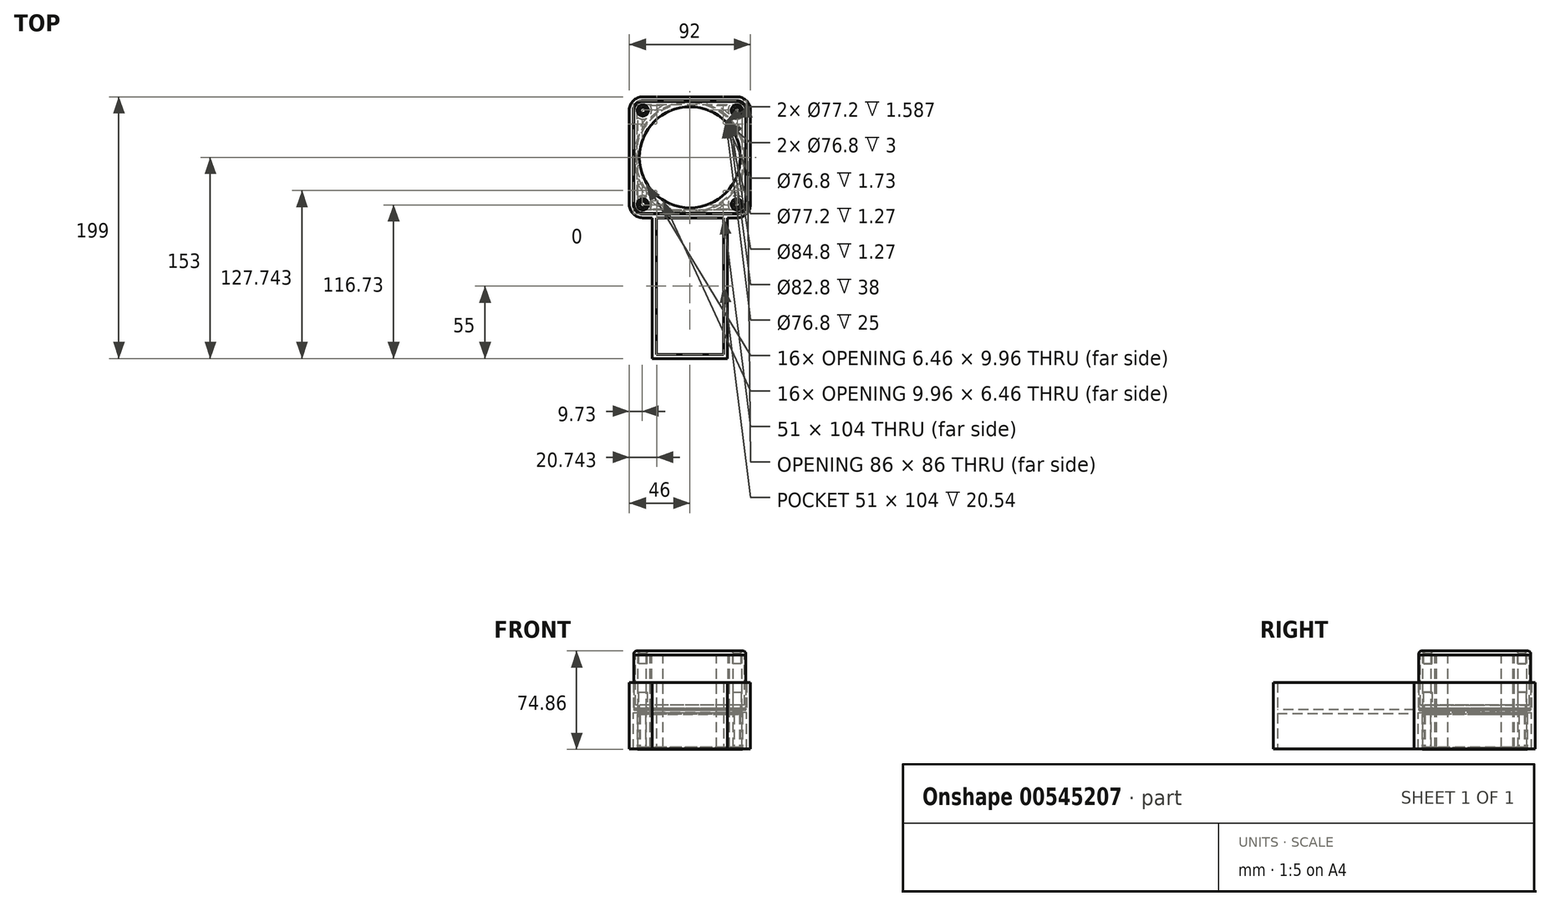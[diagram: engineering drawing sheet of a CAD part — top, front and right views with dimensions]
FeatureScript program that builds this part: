
annotation { "Feature Type Name" : "Feature", "Feature Type Description" : "" }
export const myFeature = defineFeature(function(context is Context, id is Id, definition is map)
    precondition{}
    {
        {
            var Q0;
            Q0=qCreatedBy(makeId("Top.planeOp"),FACE);
            var sketch = newSketch(context, id + "F0", { "sketchPlane" : qUnion([Q0])});
            skCircle(sketch, "E0", {"center": v(0, 0) * mm, "radius": 38.4 * mm});
            skLineSegment(sketch, "E1.bottom", {"start": v(40, -40) * mm, "end": v(-40, -40) * mm});
            skLineSegment(sketch, "E1.top", {"start": v(40, 40) * mm, "end": v(-40, 40) * mm});
            skLineSegment(sketch, "E1.left", {"start": v(40, -40) * mm, "end": v(40, 40) * mm});
            skLineSegment(sketch, "E1.right", {"start": v(-40, -40) * mm, "end": v(-40, 40) * mm});
            skLineSegment(sketch, "E2", {"start": v(0, 36.26) * mm, "end": v(0, 0) * mm, "construction": true});
            skLineSegment(sketch, "E3", {"start": v(0, 0) * mm, "end": v(31.67, 0) * mm, "construction": true});
            skCircle(sketch, "E4", {"center": v(-35.75, 35.75) * mm, "radius": 2.1 * mm});
            skCircle(sketch, "E5.MirrorC", {"center": v(35.75, 35.75) * mm, "radius": 2.1 * mm});
            skCircle(sketch, "E6.MirrorC", {"center": v(35.75, -35.75) * mm, "radius": 2.1 * mm});
            skCircle(sketch, "E7.MirrorC", {"center": v(-35.75, -35.75) * mm, "radius": 2.1 * mm});
            skSolve(sketch);
        }
        {
            var Q0;
            Q0 = qSketchRegion(id + "F0", true);
            extrude(context, id + "F1", {"entities" : qUnion([Q0]), "depth" : 25 * mm, "offsetDistance" : 25 * mm});
        }
        {
            var Q0;
            Q0=makeQuery(id+"F1.opExtrude","CAP_FACE",FACE,{"disambiguationData":[OSD([sQuery(id+"F0.wireOp",EDGE,"E0"),sQuery(id+"F0.wireOp",EDGE,"E1.bottom"),sQuery(id+"F0.wireOp",EDGE,"E1.top"),sQuery(id+"F0.wireOp",EDGE,"E1.left"),sQuery(id+"F0.wireOp",EDGE,"E1.right"),sQuery(id+"F0.wireOp",EDGE,"E4"),sQuery(id+"F0.wireOp",EDGE,"E5.MirrorC"),sQuery(id+"F0.wireOp",EDGE,"E6.MirrorC"),sQuery(id+"F0.wireOp",EDGE,"E7.MirrorC")])],"isStart":false});
            var sketch = newSketch(context, id + "F2", { "sketchPlane" : qUnion([Q0])});
            skCircle(sketch, "E8.0", {"center": v(0, 0) * mm, "radius": 38.6 * mm});
            skLineSegment(sketch, "E9.0", {"start": v(39.8, -39.8) * mm, "end": v(39.8, 39.8) * mm});
            skLineSegment(sketch, "E9.1", {"start": v(-39.8, -39.8) * mm, "end": v(39.8, -39.8) * mm});
            skLineSegment(sketch, "E9.2", {"start": v(-39.8, 39.8) * mm, "end": v(-39.8, -39.8) * mm});
            skLineSegment(sketch, "E9.3", {"start": v(39.8, 39.8) * mm, "end": v(-39.8, 39.8) * mm});
            skCircle(sketch, "E10.0", {"center": v(-35.75, 35.75) * mm, "radius": 2.3 * mm});
            skCircle(sketch, "E11.0", {"center": v(35.75, 35.75) * mm, "radius": 2.3 * mm});
            skCircle(sketch, "E12.0", {"center": v(35.75, -35.75) * mm, "radius": 2.3 * mm});
            skCircle(sketch, "E13.0", {"center": v(-35.75, -35.75) * mm, "radius": 2.3 * mm});
            skSolve(sketch);
        }
        {
            var Q0;
            Q0 = qSketchRegion(id + "F2", true);
            extrude(context, id + "F3", {"entities" : qUnion([Q0]), "depth" : 1.59 * mm, "offsetDistance" : 25 * mm});
        }
        {
            var Q0;
            Q0=makeQuery(id+"F1.opExtrude","CAP_FACE",FACE,{"disambiguationData":[OSD([sQuery(id+"F0.wireOp",EDGE,"E0"),sQuery(id+"F0.wireOp",EDGE,"E1.bottom"),sQuery(id+"F0.wireOp",EDGE,"E1.top"),sQuery(id+"F0.wireOp",EDGE,"E1.left"),sQuery(id+"F0.wireOp",EDGE,"E1.right"),sQuery(id+"F0.wireOp",EDGE,"E4"),sQuery(id+"F0.wireOp",EDGE,"E5.MirrorC"),sQuery(id+"F0.wireOp",EDGE,"E6.MirrorC"),sQuery(id+"F0.wireOp",EDGE,"E7.MirrorC")])],"isStart":true});
            var sketch = newSketch(context, id + "F4", { "sketchPlane" : qUnion([Q0])});
            skCircle(sketch, "E14.0", {"center": v(0, 0) * mm, "radius": 38.6 * mm});
            skLineSegment(sketch, "E14.1", {"start": v(39.8, 39.8) * mm, "end": v(39.8, -39.8) * mm});
            skLineSegment(sketch, "E14.2", {"start": v(-39.8, 39.8) * mm, "end": v(39.8, 39.8) * mm});
            skLineSegment(sketch, "E14.3", {"start": v(-39.8, -39.8) * mm, "end": v(-39.8, 39.8) * mm});
            skLineSegment(sketch, "E14.4", {"start": v(39.8, -39.8) * mm, "end": v(-39.8, -39.8) * mm});
            skCircle(sketch, "E14.5", {"center": v(-35.75, -35.75) * mm, "radius": 2.3 * mm});
            skCircle(sketch, "E14.6", {"center": v(35.75, -35.75) * mm, "radius": 2.3 * mm});
            skCircle(sketch, "E14.7", {"center": v(35.75, 35.75) * mm, "radius": 2.3 * mm});
            skCircle(sketch, "E14.8", {"center": v(-35.75, 35.75) * mm, "radius": 2.3 * mm});
            skSolve(sketch);
        }
        {
            var Q0;
            Q0 = qSketchRegion(id + "F4", true);
            extrude(context, id + "F5", {"entities" : qUnion([Q0]), "depth" : 1.59 * mm, "offsetDistance" : 25 * mm});
        }
        {
            var Q0;
            Q0=makeQuery(id+"F3.opExtrude","CAP_FACE",FACE,{"disambiguationData":[OSD([sQuery(id+"F2.wireOp",EDGE,"E8.0"),sQuery(id+"F2.wireOp",EDGE,"E9.0"),sQuery(id+"F2.wireOp",EDGE,"E9.1"),sQuery(id+"F2.wireOp",EDGE,"E9.2"),sQuery(id+"F2.wireOp",EDGE,"E9.3"),sQuery(id+"F2.wireOp",EDGE,"E10.0"),sQuery(id+"F2.wireOp",EDGE,"E11.0"),sQuery(id+"F2.wireOp",EDGE,"E12.0"),sQuery(id+"F2.wireOp",EDGE,"E13.0")])],"isStart":false});
            cPlane(context, id + "F6", {"entities" : qUnion([Q0]), "cplaneType" : CPlaneType.OFFSET, "offset" : 0.32 * mm, "oppositeDirection" : true, "width" : 150 * mm, "height" : 150 * mm});
        }
        {
            var Q0;
            Q0=makeQuery(id+"F5.opExtrude","CAP_FACE",FACE,{"disambiguationData":[OSD([sQuery(id+"F4.wireOp",EDGE,"E14.0"),sQuery(id+"F4.wireOp",EDGE,"E14.1"),sQuery(id+"F4.wireOp",EDGE,"E14.2"),sQuery(id+"F4.wireOp",EDGE,"E14.3"),sQuery(id+"F4.wireOp",EDGE,"E14.4"),sQuery(id+"F4.wireOp",EDGE,"E14.5"),sQuery(id+"F4.wireOp",EDGE,"E14.6"),sQuery(id+"F4.wireOp",EDGE,"E14.7"),sQuery(id+"F4.wireOp",EDGE,"E14.8")])],"isStart":false});
            cPlane(context, id + "F7", {"entities" : qUnion([Q0]), "cplaneType" : CPlaneType.OFFSET, "offset" : 0.32 * mm, "oppositeDirection" : true, "width" : 150 * mm, "height" : 150 * mm});
        }
        {
            var Q0;
            Q0=qCreatedBy(id+"F6.planeOp",FACE);
            var sketch = newSketch(context, id + "F8", { "sketchPlane" : qUnion([Q0])});
            skLineSegment(sketch, "E15.bottom", {"start": v(-43, 43) * mm, "end": v(43, 43) * mm});
            skLineSegment(sketch, "E15.top", {"start": v(-43, -43) * mm, "end": v(43, -43) * mm});
            skLineSegment(sketch, "E15.left", {"start": v(-43, 43) * mm, "end": v(-43, -43) * mm});
            skLineSegment(sketch, "E15.right", {"start": v(43, 43) * mm, "end": v(43, -43) * mm});
            skPoint(sketch, "E15.middle", {"position": v(0, 0) * mm});
            skLineSegment(sketch, "E16.0", {"start": v(-46, 46) * mm, "end": v(46, 46) * mm});
            skLineSegment(sketch, "E16.1", {"start": v(-46, 46) * mm, "end": v(-46, -46) * mm});
            skLineSegment(sketch, "E16.2", {"start": v(-46, -46) * mm, "end": v(46, -46) * mm});
            skLineSegment(sketch, "E16.3", {"start": v(46, 46) * mm, "end": v(46, -46) * mm});
            skSolve(sketch);
        }
        {
            var Q0;
            Q0 = qSketchRegion(id + "F8", true);
            var Q1;
            Q1=qCreatedBy(id+"F7.planeOp",FACE);
            extrude(context, id + "F9", {"entities" : qUnion([Q0]), "endBound" : BoundingType.UP_TO_SURFACE, "oppositeDirection" : true, "depth" : 3 * mm, "endBoundEntityFace" : qUnion([Q1]), "offsetDistance" : 25 * mm});
        }
        {
            var Q0;
            Q0=makeQuery(id+"F9.opExtrude","CAP_FACE",FACE,{"disambiguationData":[OSD([sQuery(id+"F8.wireOp",EDGE,"E15.bottom"),sQuery(id+"F8.wireOp",EDGE,"E15.top"),sQuery(id+"F8.wireOp",EDGE,"E15.left"),sQuery(id+"F8.wireOp",EDGE,"E15.right"),sQuery(id+"F8.wireOp",EDGE,"E16.0"),sQuery(id+"F8.wireOp",EDGE,"E16.1"),sQuery(id+"F8.wireOp",EDGE,"E16.2"),sQuery(id+"F8.wireOp",EDGE,"E16.3")])],"isStart":true});
            var sketch = newSketch(context, id + "F10", { "sketchPlane" : qUnion([Q0])});
            skCircle(sketch, "E17.0", {"center": v(0, 0) * mm, "radius": 38.4 * mm});
            skLineSegment(sketch, "E18.0", {"start": v(-46, 46) * mm, "end": v(-46, -46) * mm});
            skLineSegment(sketch, "E18.1", {"start": v(-46, 46) * mm, "end": v(46, 46) * mm});
            skLineSegment(sketch, "E18.2", {"start": v(46, 46) * mm, "end": v(46, -46) * mm});
            skLineSegment(sketch, "E18.3", {"start": v(-46, -46) * mm, "end": v(46, -46) * mm});
            skCircle(sketch, "E19.0", {"center": v(0, 0) * mm, "radius": 41.4 * mm, "construction": true});
            skCircle(sketch, "E20.0", {"center": v(-35.75, 35.75) * mm, "radius": 2.3 * mm});
            skCircle(sketch, "E20.1", {"center": v(35.75, 35.75) * mm, "radius": 2.3 * mm});
            skCircle(sketch, "E20.2", {"center": v(35.75, -35.75) * mm, "radius": 2.3 * mm});
            skCircle(sketch, "E20.3", {"center": v(-35.75, -35.75) * mm, "radius": 2.3 * mm});
            skSolve(sketch);
        }
        {
            var Q0;
            Q0 = qSketchRegion(id + "F10", true);
            extrude(context, id + "F11", {"entities" : qUnion([Q0]), "operationType" : NewBodyOperationType.ADD, "depth" : 3 * mm, "offsetDistance" : 25 * mm});
        }
        {
            var Q0;
            Q0=makeQuery(id+"F11.opExtrude","CAP_EDGE",EDGE,{"disambiguationData":[OSD([sQuery(id+"F10.wireOp",EDGE,"E20.1")])],"isStart":false});
            var Q1;
            Q1=makeQuery(id+"F11.opExtrude","CAP_EDGE",EDGE,{"disambiguationData":[OSD([sQuery(id+"F10.wireOp",EDGE,"E20.2")])],"isStart":false});
            var Q2;
            Q2=makeQuery(id+"F11.opExtrude","CAP_EDGE",EDGE,{"disambiguationData":[OSD([sQuery(id+"F10.wireOp",EDGE,"E20.3")])],"isStart":false});
            var Q3;
            Q3=makeQuery(id+"F11.opExtrude","CAP_EDGE",EDGE,{"disambiguationData":[OSD([sQuery(id+"F10.wireOp",EDGE,"E20.0")])],"isStart":false});
            chamfer(context, id + "F12", {"entities" : qUnion([Q0, Q1, Q2, Q3]), "width" : 2 * mm, "tangentPropagation" : true});
        }
        {
            var Q0;
            Q0=makeQuery(id+"F11.opExtrude","CAP_FACE",FACE,{"disambiguationData":[OSD([sQuery(id+"F10.wireOp",EDGE,"E17.0"),sQuery(id+"F10.wireOp",EDGE,"E18.0"),sQuery(id+"F10.wireOp",EDGE,"E18.1"),sQuery(id+"F10.wireOp",EDGE,"E18.2"),sQuery(id+"F10.wireOp",EDGE,"E18.3"),sQuery(id+"F10.wireOp",EDGE,"E20.0"),sQuery(id+"F10.wireOp",EDGE,"E20.1"),sQuery(id+"F10.wireOp",EDGE,"E20.2"),sQuery(id+"F10.wireOp",EDGE,"E20.3")])],"isStart":false});
            var sketch = newSketch(context, id + "F13", { "sketchPlane" : qUnion([Q0])});
            skLineSegment(sketch, "E21.0.0", {"start": v(46, -46) * mm, "end": v(46, 46) * mm});
            skLineSegment(sketch, "E21.0.1", {"start": v(46, 46) * mm, "end": v(-46, 46) * mm});
            skLineSegment(sketch, "E21.0.2", {"start": v(-46, 46) * mm, "end": v(-46, -46) * mm});
            skLineSegment(sketch, "E21.0.3", {"start": v(-46, -46) * mm, "end": v(46, -46) * mm});
            skLineSegment(sketch, "E22.0", {"start": v(43, -43) * mm, "end": v(43, 43) * mm});
            skLineSegment(sketch, "E22.1", {"start": v(-43, -43) * mm, "end": v(43, -43) * mm});
            skLineSegment(sketch, "E22.2", {"start": v(-43, 43) * mm, "end": v(-43, -43) * mm});
            skLineSegment(sketch, "E22.3", {"start": v(43, 43) * mm, "end": v(-43, 43) * mm});
            skSolve(sketch);
        }
        {
            var Q0;
            Q0 = qSketchRegion(id + "F13", true);
            extrude(context, id + "F14", {"entities" : qUnion([Q0]), "operationType" : NewBodyOperationType.ADD, "depth" : 20 * mm, "offsetDistance" : 25 * mm});
        }
        {
            var Q0;
            Q0=makeQuery(id+"F11.opExtrude","CAP_FACE",FACE,{"disambiguationData":[OSD([sQuery(id+"F10.wireOp",EDGE,"E17.0"),sQuery(id+"F10.wireOp",EDGE,"E18.0"),sQuery(id+"F10.wireOp",EDGE,"E18.1"),sQuery(id+"F10.wireOp",EDGE,"E18.2"),sQuery(id+"F10.wireOp",EDGE,"E18.3"),sQuery(id+"F10.wireOp",EDGE,"E20.0"),sQuery(id+"F10.wireOp",EDGE,"E20.1"),sQuery(id+"F10.wireOp",EDGE,"E20.2"),sQuery(id+"F10.wireOp",EDGE,"E20.3")])],"isStart":false});
            var sketch = newSketch(context, id + "F15", { "sketchPlane" : qUnion([Q0])});
            skCircle(sketch, "E23.0", {"center": v(0, 0) * mm, "radius": 38.4 * mm});
            skCircle(sketch, "E24.0", {"center": v(0, 0) * mm, "radius": 42.4 * mm});
            skSolve(sketch);
        }
        {
            var Q0;
            Q0 = qSketchRegion(id + "F15", true);
            extrude(context, id + "F16", {"entities" : qUnion([Q0]), "operationType" : NewBodyOperationType.REMOVE, "oppositeDirection" : true, "depth" : 1.59 * mm - 0.32 * mm, "offsetDistance" : 25 * mm});
        }
        {
            var Q0;
            Q0=makeQuery(id+"F16.boolean.opBoolean","COPY",FACE,{"derivedFrom":makeQuery(id+"F16.opExtrude","CAP_FACE",FACE,{"disambiguationData":[OSD([sQuery(id+"F15.wireOp",EDGE,"E23.0"),sQuery(id+"F15.wireOp",EDGE,"E24.0")])],"isStart":false})});
            var sketch = newSketch(context, id + "F17", { "sketchPlane" : qUnion([Q0])});
            skCircle(sketch, "E25.0", {"center": v(0, 0) * mm, "radius": 42.2 * mm});
            skCircle(sketch, "E26.0", {"center": v(0, 0) * mm, "radius": 38.6 * mm});
            skSolve(sketch);
        }
        {
            var Q0;
            Q0 = qSketchRegion(id + "F17", true);
            extrude(context, id + "F18", {"entities" : qUnion([Q0]), "depth" : 1.59 * mm, "offsetDistance" : 25 * mm});
        }
        {
            var Q0;
            Q0=makeQuery(id+"F11.opExtrude","CAP_FACE",FACE,{"disambiguationData":[OSD([sQuery(id+"F10.wireOp",EDGE,"E17.0"),sQuery(id+"F10.wireOp",EDGE,"E18.0"),sQuery(id+"F10.wireOp",EDGE,"E18.1"),sQuery(id+"F10.wireOp",EDGE,"E18.2"),sQuery(id+"F10.wireOp",EDGE,"E18.3"),sQuery(id+"F10.wireOp",EDGE,"E20.0"),sQuery(id+"F10.wireOp",EDGE,"E20.1"),sQuery(id+"F10.wireOp",EDGE,"E20.2"),sQuery(id+"F10.wireOp",EDGE,"E20.3")])],"isStart":false});
            var sketch = newSketch(context, id + "F19", { "sketchPlane" : qUnion([Q0])});
            skLineSegment(sketch, "E27.0", {"start": v(42.5, -42.5) * mm, "end": v(42.5, 42.5) * mm});
            skLineSegment(sketch, "E27.1", {"start": v(-42.5, -42.5) * mm, "end": v(42.5, -42.5) * mm});
            skLineSegment(sketch, "E27.2", {"start": v(-42.5, 42.5) * mm, "end": v(-42.5, -42.5) * mm});
            skLineSegment(sketch, "E27.3", {"start": v(42.5, 42.5) * mm, "end": v(-42.5, 42.5) * mm});
            skCircle(sketch, "E28.0", {"center": v(0, 0) * mm, "radius": 38.4 * mm});
            skSolve(sketch);
        }
        {
            var Q0;
            Q0 = qSketchRegion(id + "F19", true);
            extrude(context, id + "F20", {"entities" : qUnion([Q0]), "depth" : 41 * mm, "offsetDistance" : 25 * mm});
        }
        {
            var Q0;
            Q0=makeQuery(id+"F20.opExtrude","CAP_FACE",FACE,{"disambiguationData":[OSD([sQuery(id+"F19.wireOp",EDGE,"E27.0"),sQuery(id+"F19.wireOp",EDGE,"E27.1"),sQuery(id+"F19.wireOp",EDGE,"E27.2"),sQuery(id+"F19.wireOp",EDGE,"E27.3"),sQuery(id+"F19.wireOp",EDGE,"E28.0")])],"isStart":false});
            var sketch = newSketch(context, id + "F21", { "sketchPlane" : qUnion([Q0])});
            skCircle(sketch, "E29.0", {"center": v(0, 0) * mm, "radius": 41.4 * mm});
            skSolve(sketch);
        }
        {
            var Q0;
            Q0 = qSketchRegion(id + "F21", true);
            extrude(context, id + "F22", {"entities" : qUnion([Q0]), "operationType" : NewBodyOperationType.REMOVE, "oppositeDirection" : true, "depth" : 38 * mm, "offsetDistance" : 25 * mm});
        }
        {
            var Q0;
            Q0=makeQuery(id+"F20.opExtrude","CAP_FACE",FACE,{"disambiguationData":[OSD([sQuery(id+"F19.wireOp",EDGE,"E27.0"),sQuery(id+"F19.wireOp",EDGE,"E27.1"),sQuery(id+"F19.wireOp",EDGE,"E27.2"),sQuery(id+"F19.wireOp",EDGE,"E27.3"),sQuery(id+"F19.wireOp",EDGE,"E28.0")])],"isStart":true});
            var sketch = newSketch(context, id + "F23", { "sketchPlane" : qUnion([Q0])});
            skCircle(sketch, "E30", {"center": v(35.75, -35.75) * mm, "radius": 3.25 * mm});
            skCircle(sketch, "E31", {"center": v(-35.75, 35.75) * mm, "radius": 3.25 * mm});
            skCircle(sketch, "E32", {"center": v(-35.75, -35.75) * mm, "radius": 3.25 * mm});
            skCircle(sketch, "E33", {"center": v(35.75, 35.75) * mm, "radius": 3.25 * mm});
            skSolve(sketch);
        }
        {
            var Q0;
            Q0 = qSketchRegion(id + "F23", true);
            extrude(context, id + "F24", {"entities" : qUnion([Q0]), "operationType" : NewBodyOperationType.REMOVE, "oppositeDirection" : true, "depth" : 12.7 * mm, "offsetDistance" : 25 * mm});
        }
        {
            var Q0;
            Q0=makeQuery(id+"F20.opExtrude","CAP_FACE",FACE,{"disambiguationData":[OSD([sQuery(id+"F19.wireOp",EDGE,"E27.0"),sQuery(id+"F19.wireOp",EDGE,"E27.1"),sQuery(id+"F19.wireOp",EDGE,"E27.2"),sQuery(id+"F19.wireOp",EDGE,"E27.3"),sQuery(id+"F19.wireOp",EDGE,"E28.0")])],"isStart":false});
            var sketch = newSketch(context, id + "F25", { "sketchPlane" : qUnion([Q0])});
            skCircle(sketch, "E34", {"center": v(-35.75, 35.75) * mm, "radius": 3.15 * mm});
            skCircle(sketch, "E35", {"center": v(35.75, 35.75) * mm, "radius": 3.15 * mm});
            skCircle(sketch, "E36", {"center": v(35.75, -35.75) * mm, "radius": 3.15 * mm});
            skCircle(sketch, "E37", {"center": v(-35.75, -35.75) * mm, "radius": 3.15 * mm});
            skSolve(sketch);
        }
        {
            var Q0;
            Q0 = qSketchRegion(id + "F25", true);
            extrude(context, id + "F26", {"entities" : qUnion([Q0]), "operationType" : NewBodyOperationType.REMOVE, "oppositeDirection" : true, "depth" : 6.7 * mm, "offsetDistance" : 25 * mm});
        }
        {
            var Q0;
            Q0=makeQuery(id+"F20.opExtrude","CAP_FACE",FACE,{"disambiguationData":[OSD([sQuery(id+"F19.wireOp",EDGE,"E27.0"),sQuery(id+"F19.wireOp",EDGE,"E27.1"),sQuery(id+"F19.wireOp",EDGE,"E27.2"),sQuery(id+"F19.wireOp",EDGE,"E27.3"),sQuery(id+"F19.wireOp",EDGE,"E28.0")])],"isStart":false});
            var sketch = newSketch(context, id + "F27", { "sketchPlane" : qUnion([Q0])});
            skCircle(sketch, "E38", {"center": v(-35.75, 35.75) * mm, "radius": 3.67 * mm});
            skCircle(sketch, "E39", {"center": v(-35.75, -35.75) * mm, "radius": 3.67 * mm});
            skCircle(sketch, "E40", {"center": v(35.75, -35.75) * mm, "radius": 3.67 * mm});
            skCircle(sketch, "E41", {"center": v(35.75, 35.75) * mm, "radius": 3.67 * mm});
            skCircle(sketch, "E42.cCircle", {"center": v(-35.75, 35.75) * mm, "radius": 3.17 * mm, "construction": true});
            skLineSegment(sketch, "E42.0", {"start": v(-33.92, 32.58) * mm, "end": v(-37.58, 32.58) * mm, "construction": true});
            skLineSegment(sketch, "E42.1", {"start": v(-37.58, 32.58) * mm, "end": v(-39.42, 35.75) * mm, "construction": true});
            skLineSegment(sketch, "E42.2", {"start": v(-39.42, 35.75) * mm, "end": v(-37.58, 38.93) * mm, "construction": true});
            skLineSegment(sketch, "E42.3", {"start": v(-37.58, 38.93) * mm, "end": v(-33.92, 38.93) * mm, "construction": true});
            skLineSegment(sketch, "E42.4", {"start": v(-33.92, 38.93) * mm, "end": v(-32.08, 35.75) * mm, "construction": true});
            skLineSegment(sketch, "E42.5", {"start": v(-32.08, 35.75) * mm, "end": v(-33.92, 32.58) * mm, "construction": true});
            skPoint(sketch, "E42.0.midPoint", {"position": v(-35.75, 32.58) * mm});
            skSolve(sketch);
        }
        {
            var Q0;
            Q0 = qSketchRegion(id + "F27", true);
            extrude(context, id + "F28", {"entities" : qUnion([Q0]), "operationType" : NewBodyOperationType.REMOVE, "oppositeDirection" : true, "depth" : .5 * mm, "offsetDistance" : 25 * mm});
        }
        {
            var Q0;
            Q0=makeQuery(id+"F20.opExtrude","CAP_FACE",FACE,{"disambiguationData":[OSD([sQuery(id+"F19.wireOp",EDGE,"E27.0"),sQuery(id+"F19.wireOp",EDGE,"E27.1"),sQuery(id+"F19.wireOp",EDGE,"E27.2"),sQuery(id+"F19.wireOp",EDGE,"E27.3"),sQuery(id+"F19.wireOp",EDGE,"E28.0")])],"isStart":false});
            var sketch = newSketch(context, id + "F29", { "sketchPlane" : qUnion([Q0])});
            skArc(sketch, "E43.0", {"start": v(-39.5, 30.24) * mm, "mid": v(-36.35, 29.11) * mm, "end": v(-33.04, 29.66) * mm});
            skLineSegment(sketch, "E44.0", {"start": v(-39.5, 30.24) * mm, "end": v(-39.5, 20.28) * mm});
            skLineSegment(sketch, "E45.trimOffspring", {"start": v(-39.5, -20.28) * mm, "end": v(-39.5, -42.5) * mm});
            skArc(sketch, "E46.trimOffspring", {"start": v(-29.66, 33.04) * mm, "mid": v(-29.11, 36.35) * mm, "end": v(-30.24, 39.5) * mm});
            skArc(sketch, "E47.trimOffspring", {"start": v(-33.04, 29.66) * mm, "mid": v(-36.57, 25.18) * mm, "end": v(-39.5, 20.28) * mm});
            skArc(sketch, "E48.trimOffspring", {"start": v(-20.28, 39.5) * mm, "mid": v(-25.18, 36.57) * mm, "end": v(-29.66, 33.04) * mm});
            skLineSegment(sketch, "E49.trimOffspring", {"start": v(-20.28, 39.5) * mm, "end": v(-30.24, 39.5) * mm});
            skArc(sketch, "E50.1.0", {"start": v(-39.5, -20.28) * mm, "mid": v(-36.57, -25.18) * mm, "end": v(-33.04, -29.66) * mm});
            skLineSegment(sketch, "E50.1.1", {"start": v(-30.24, -39.5) * mm, "end": v(-20.28, -39.5) * mm});
            skArc(sketch, "E50.1.2", {"start": v(-30.24, -39.5) * mm, "mid": v(-29.11, -36.35) * mm, "end": v(-29.66, -33.04) * mm});
            skArc(sketch, "E50.1.3", {"start": v(-29.66, -33.04) * mm, "mid": v(-25.18, -36.57) * mm, "end": v(-20.28, -39.5) * mm});
            skArc(sketch, "E50.1.4", {"start": v(-33.04, -29.66) * mm, "mid": v(-36.35, -29.11) * mm, "end": v(-39.5, -30.24) * mm});
            skLineSegment(sketch, "E50.1.5", {"start": v(-39.5, -20.28) * mm, "end": v(-39.5, -30.24) * mm});
            skArc(sketch, "E50.2.0", {"start": v(20.28, -39.5) * mm, "mid": v(25.18, -36.57) * mm, "end": v(29.66, -33.04) * mm});
            skLineSegment(sketch, "E50.2.1", {"start": v(39.5, -30.24) * mm, "end": v(39.5, -20.28) * mm});
            skArc(sketch, "E50.2.2", {"start": v(39.5, -30.24) * mm, "mid": v(36.35, -29.11) * mm, "end": v(33.04, -29.66) * mm});
            skArc(sketch, "E50.2.3", {"start": v(33.04, -29.66) * mm, "mid": v(36.57, -25.18) * mm, "end": v(39.5, -20.28) * mm});
            skArc(sketch, "E50.2.4", {"start": v(29.66, -33.04) * mm, "mid": v(29.11, -36.35) * mm, "end": v(30.24, -39.5) * mm});
            skLineSegment(sketch, "E50.2.5", {"start": v(20.28, -39.5) * mm, "end": v(30.24, -39.5) * mm});
            skArc(sketch, "E50.3.0", {"start": v(39.5, 20.28) * mm, "mid": v(36.57, 25.18) * mm, "end": v(33.04, 29.66) * mm});
            skLineSegment(sketch, "E50.3.1", {"start": v(30.24, 39.5) * mm, "end": v(20.28, 39.5) * mm});
            skArc(sketch, "E50.3.2", {"start": v(30.24, 39.5) * mm, "mid": v(29.11, 36.35) * mm, "end": v(29.66, 33.04) * mm});
            skArc(sketch, "E50.3.3", {"start": v(29.66, 33.04) * mm, "mid": v(25.18, 36.57) * mm, "end": v(20.28, 39.5) * mm});
            skArc(sketch, "E50.3.4", {"start": v(33.04, 29.66) * mm, "mid": v(36.35, 29.11) * mm, "end": v(39.5, 30.24) * mm});
            skLineSegment(sketch, "E50.3.5", {"start": v(39.5, 20.28) * mm, "end": v(39.5, 30.24) * mm});
            skSolve(sketch);
        }
        {
            var Q0;
            Q0 = qSketchRegion(id + "F29", true);
            extrude(context, id + "F30", {"entities" : qUnion([Q0]), "operationType" : NewBodyOperationType.REMOVE, "endBound" : BoundingType.THROUGH_ALL, "oppositeDirection" : true, "depth" : 38 * mm, "offsetDistance" : 25 * mm});
        }
        {
            var Q0;
            Q0=makeQuery(id+"F20.opExtrude","SWEPT_EDGE",EDGE,{"disambiguationData":[OSD([sQuery(id+"F19.wireOp",EDGE,"E27.0"),sQuery(id+"F19.wireOp",EDGE,"E27.1")])]});
            var Q1;
            Q1=makeQuery(id+"F20.opExtrude","SWEPT_EDGE",EDGE,{"disambiguationData":[OSD([sQuery(id+"F19.wireOp",EDGE,"E27.1"),sQuery(id+"F19.wireOp",EDGE,"E27.2")])]});
            var Q2;
            Q2=makeQuery(id+"F20.opExtrude","SWEPT_EDGE",EDGE,{"disambiguationData":[OSD([sQuery(id+"F19.wireOp",EDGE,"E27.0"),sQuery(id+"F19.wireOp",EDGE,"E27.3")])]});
            var Q3;
            Q3=makeQuery(id+"F20.opExtrude","SWEPT_EDGE",EDGE,{"disambiguationData":[OSD([sQuery(id+"F19.wireOp",EDGE,"E27.2"),sQuery(id+"F19.wireOp",EDGE,"E27.3")])]});
            fillet(context, id + "F31", {"entities" : qUnion([Q0, Q1, Q2, Q3]), "radius" : 6.6 * mm, "tangentPropagation" : true, "allowEdgeOverflow" : false});
        }
        {
            var Q0;
            Q0=makeQuery(id+"F20.opExtrude","CAP_EDGE",EDGE,{"disambiguationData":[OSD([sQuery(id+"F19.wireOp",EDGE,"E27.3")])],"isStart":true});
            fillet(context, id + "F32", {"entities" : qUnion([Q0]), "radius" : 2 * mm, "tangentPropagation" : true, "allowEdgeOverflow" : false});
        }
        {
            var Q0;
            Q0=makeQuery(id+"F20.opExtrude","CAP_FACE",FACE,{"disambiguationData":[OSD([sQuery(id+"F19.wireOp",EDGE,"E27.0"),sQuery(id+"F19.wireOp",EDGE,"E27.1"),sQuery(id+"F19.wireOp",EDGE,"E27.2"),sQuery(id+"F19.wireOp",EDGE,"E27.3"),sQuery(id+"F19.wireOp",EDGE,"E28.0")])],"isStart":false});
            var sketch = newSketch(context, id + "F33", { "sketchPlane" : qUnion([Q0])});
            skLineSegment(sketch, "E51.0.0", {"start": v(42.5, -35.9) * mm, "end": v(42.5, 35.9) * mm});
            skArc(sketch, "E51.0.1", {"start": v(42.5, 35.9) * mm, "mid": v(40.57, 40.57) * mm, "end": v(35.9, 42.5) * mm});
            skLineSegment(sketch, "E51.0.2", {"start": v(35.9, 42.5) * mm, "end": v(-35.9, 42.5) * mm});
            skArc(sketch, "E51.0.3", {"start": v(-35.9, 42.5) * mm, "mid": v(-40.57, 40.57) * mm, "end": v(-42.5, 35.9) * mm});
            skLineSegment(sketch, "E51.0.4", {"start": v(-42.5, 35.9) * mm, "end": v(-42.5, -35.9) * mm});
            skArc(sketch, "E51.0.5", {"start": v(-42.5, -35.9) * mm, "mid": v(-40.57, -40.57) * mm, "end": v(-35.9, -42.5) * mm});
            skLineSegment(sketch, "E51.0.6", {"start": v(-35.9, -42.5) * mm, "end": v(35.9, -42.5) * mm});
            skArc(sketch, "E51.0.7", {"start": v(35.9, -42.5) * mm, "mid": v(40.57, -40.57) * mm, "end": v(42.5, -35.9) * mm});
            skCircle(sketch, "E52.0", {"center": v(-35.75, 35.75) * mm, "radius": 2.3 * mm});
            skCircle(sketch, "E52.1", {"center": v(-35.75, -35.75) * mm, "radius": 2.3 * mm});
            skCircle(sketch, "E52.2", {"center": v(35.75, -35.75) * mm, "radius": 2.3 * mm});
            skCircle(sketch, "E52.3", {"center": v(35.75, 35.75) * mm, "radius": 2.3 * mm});
            skCircle(sketch, "E53.0", {"center": v(0, 0) * mm, "radius": 38.4 * mm});
            skSolve(sketch);
        }
        {
            var Q0;
            Q0 = qSketchRegion(id + "F33", true);
            extrude(context, id + "F34", {"entities" : qUnion([Q0]), "depth" : 3 * mm, "offsetDistance" : 25 * mm});
        }
        {
            var Q0;
            Q0=makeQuery(id+"F34.opExtrude","CAP_EDGE",EDGE,{"disambiguationData":[OSD([sQuery(id+"F33.wireOp",EDGE,"E52.3")])],"isStart":false});
            var Q1;
            Q1=makeQuery(id+"F34.opExtrude","CAP_EDGE",EDGE,{"disambiguationData":[OSD([sQuery(id+"F33.wireOp",EDGE,"E52.0")])],"isStart":false});
            var Q2;
            Q2=makeQuery(id+"F34.opExtrude","CAP_EDGE",EDGE,{"disambiguationData":[OSD([sQuery(id+"F33.wireOp",EDGE,"E52.1")])],"isStart":false});
            var Q3;
            Q3=makeQuery(id+"F34.opExtrude","CAP_EDGE",EDGE,{"disambiguationData":[OSD([sQuery(id+"F33.wireOp",EDGE,"E52.2")])],"isStart":false});
            chamfer(context, id + "F35", {"entities" : qUnion([Q0, Q1, Q2, Q3]), "width" : 2 * mm, "tangentPropagation" : true});
        }
        {
            var Q0;
            Q0=makeQuery(id+"F34.opExtrude","CAP_EDGE",EDGE,{"disambiguationData":[OSD([sQuery(id+"F33.wireOp",EDGE,"E51.0.0")])],"isStart":false});
            fillet(context, id + "F36", {"entities" : qUnion([Q0]), "radius" : 2 * mm, "tangentPropagation" : true, "allowEdgeOverflow" : false});
        }
        {
            var Q0;
            Q0=makeQuery(id+"F14.opExtrude","SWEPT_EDGE",EDGE,{"disambiguationData":[OSD([sQuery(id+"F13.wireOp",EDGE,"E22.1"),sQuery(id+"F13.wireOp",EDGE,"E22.2")])]});
            var Q1;
            Q1=makeQuery(id+"F14.opExtrude","SWEPT_EDGE",EDGE,{"disambiguationData":[OSD([sQuery(id+"F13.wireOp",EDGE,"E22.2"),sQuery(id+"F13.wireOp",EDGE,"E22.3")])]});
            var Q2;
            Q2=makeQuery(id+"F14.opExtrude","SWEPT_EDGE",EDGE,{"disambiguationData":[OSD([sQuery(id+"F13.wireOp",EDGE,"E22.0"),sQuery(id+"F13.wireOp",EDGE,"E22.3")])]});
            var Q3;
            Q3=makeQuery(id+"F14.opExtrude","SWEPT_EDGE",EDGE,{"disambiguationData":[OSD([sQuery(id+"F13.wireOp",EDGE,"E22.0"),sQuery(id+"F13.wireOp",EDGE,"E22.1")])]});
            fillet(context, id + "F37", {"entities" : qUnion([Q0, Q1, Q2, Q3]), "radius" : 7.1 * mm, "tangentPropagation" : true, "allowEdgeOverflow" : false});
        }
        {
            var Q0;
            Q0=makeQuery(id+"F14.boolean.opBoolean","MERGE",EDGE,{"derivedFrom":[makeQuery(id+"F11.boolean.opBoolean","MERGE",EDGE,{"derivedFrom":[makeQuery(id+"F9.opExtrude","SWEPT_EDGE",EDGE,{"disambiguationData":[OSD([sQuery(id+"F8.wireOp",EDGE,"E16.2"),sQuery(id+"F8.wireOp",EDGE,"E16.3")])]}),makeQuery(id+"F11.opExtrude","SWEPT_EDGE",EDGE,{"disambiguationData":[OSD([sQuery(id+"F10.wireOp",EDGE,"E18.2"),sQuery(id+"F10.wireOp",EDGE,"E18.3")])]})]}),makeQuery(id+"F14.opExtrude","SWEPT_EDGE",EDGE,{"disambiguationData":[OSD([sQuery(id+"F13.wireOp",EDGE,"E21.0.0"),sQuery(id+"F13.wireOp",EDGE,"E21.0.3")])]})]});
            var Q1;
            Q1=makeQuery(id+"F14.boolean.opBoolean","MERGE",EDGE,{"derivedFrom":[makeQuery(id+"F11.boolean.opBoolean","MERGE",EDGE,{"derivedFrom":[makeQuery(id+"F9.opExtrude","SWEPT_EDGE",EDGE,{"disambiguationData":[OSD([sQuery(id+"F8.wireOp",EDGE,"E16.0"),sQuery(id+"F8.wireOp",EDGE,"E16.3")])]}),makeQuery(id+"F11.opExtrude","SWEPT_EDGE",EDGE,{"disambiguationData":[OSD([sQuery(id+"F10.wireOp",EDGE,"E18.1"),sQuery(id+"F10.wireOp",EDGE,"E18.2")])]})]}),makeQuery(id+"F14.opExtrude","SWEPT_EDGE",EDGE,{"disambiguationData":[OSD([sQuery(id+"F13.wireOp",EDGE,"E21.0.0"),sQuery(id+"F13.wireOp",EDGE,"E21.0.1")])]})]});
            var Q2;
            Q2=makeQuery(id+"F14.boolean.opBoolean","MERGE",EDGE,{"derivedFrom":[makeQuery(id+"F11.boolean.opBoolean","MERGE",EDGE,{"derivedFrom":[makeQuery(id+"F9.opExtrude","SWEPT_EDGE",EDGE,{"disambiguationData":[OSD([sQuery(id+"F8.wireOp",EDGE,"E16.0"),sQuery(id+"F8.wireOp",EDGE,"E16.1")])]}),makeQuery(id+"F11.opExtrude","SWEPT_EDGE",EDGE,{"disambiguationData":[OSD([sQuery(id+"F10.wireOp",EDGE,"E18.0"),sQuery(id+"F10.wireOp",EDGE,"E18.1")])]})]}),makeQuery(id+"F14.opExtrude","SWEPT_EDGE",EDGE,{"disambiguationData":[OSD([sQuery(id+"F13.wireOp",EDGE,"E21.0.1"),sQuery(id+"F13.wireOp",EDGE,"E21.0.2")])]})]});
            var Q3;
            Q3=makeQuery(id+"F14.boolean.opBoolean","MERGE",EDGE,{"derivedFrom":[makeQuery(id+"F11.boolean.opBoolean","MERGE",EDGE,{"derivedFrom":[makeQuery(id+"F9.opExtrude","SWEPT_EDGE",EDGE,{"disambiguationData":[OSD([sQuery(id+"F8.wireOp",EDGE,"E16.1"),sQuery(id+"F8.wireOp",EDGE,"E16.2")])]}),makeQuery(id+"F11.opExtrude","SWEPT_EDGE",EDGE,{"disambiguationData":[OSD([sQuery(id+"F10.wireOp",EDGE,"E18.0"),sQuery(id+"F10.wireOp",EDGE,"E18.3")])]})]}),makeQuery(id+"F14.opExtrude","SWEPT_EDGE",EDGE,{"disambiguationData":[OSD([sQuery(id+"F13.wireOp",EDGE,"E21.0.2"),sQuery(id+"F13.wireOp",EDGE,"E21.0.3")])]})]});
            fillet(context, id + "F38", {"entities" : qUnion([Q0, Q1, Q2, Q3]), "radius" : 10.1 * mm, "tangentPropagation" : true, "allowEdgeOverflow" : false});
        }
        {
            var Q0;
            Q0=makeQuery(id+"F9.opExtrude","SWEPT_EDGE",EDGE,{"disambiguationData":[OSD([sQuery(id+"F8.wireOp",EDGE,"E15.top"),sQuery(id+"F8.wireOp",EDGE,"E15.left")])]});
            var Q1;
            Q1=makeQuery(id+"F9.opExtrude","SWEPT_EDGE",EDGE,{"disambiguationData":[OSD([sQuery(id+"F8.wireOp",EDGE,"E15.top"),sQuery(id+"F8.wireOp",EDGE,"E15.right")])]});
            var Q2;
            Q2=makeQuery(id+"F9.opExtrude","SWEPT_EDGE",EDGE,{"disambiguationData":[OSD([sQuery(id+"F8.wireOp",EDGE,"E15.bottom"),sQuery(id+"F8.wireOp",EDGE,"E15.left")])]});
            var Q3;
            Q3=makeQuery(id+"F9.opExtrude","SWEPT_EDGE",EDGE,{"disambiguationData":[OSD([sQuery(id+"F8.wireOp",EDGE,"E15.bottom"),sQuery(id+"F8.wireOp",EDGE,"E15.right")])]});
            fillet(context, id + "F39", {"entities" : qUnion([Q0, Q1, Q2, Q3]), "radius" : 7.1 * mm, "tangentPropagation" : true, "allowEdgeOverflow" : false});
        }
        {
            var Q0;
            Q0=makeQuery(id+"F9.opExtrude","CAP_FACE",FACE,{"disambiguationData":[OSD([sQuery(id+"F8.wireOp",EDGE,"E15.bottom"),sQuery(id+"F8.wireOp",EDGE,"E15.top"),sQuery(id+"F8.wireOp",EDGE,"E15.left"),sQuery(id+"F8.wireOp",EDGE,"E15.right"),sQuery(id+"F8.wireOp",EDGE,"E16.0"),sQuery(id+"F8.wireOp",EDGE,"E16.1"),sQuery(id+"F8.wireOp",EDGE,"E16.2"),sQuery(id+"F8.wireOp",EDGE,"E16.3")])],"isStart":false});
            var sketch = newSketch(context, id + "F40", { "sketchPlane" : qUnion([Q0])});
            skLineSegment(sketch, "E54", {"start": v(0, 0) * mm, "end": v(0, 161.3) * mm, "construction": true});
            skLineSegment(sketch, "E55.bottom", {"start": v(-25.5, 46) * mm, "end": v(25.5, 46) * mm, "construction": true});
            skLineSegment(sketch, "E55.top", {"start": v(-25.5, 138) * mm, "end": v(25.5, 138) * mm, "construction": true});
            skLineSegment(sketch, "E55.left", {"start": v(-25.5, 46) * mm, "end": v(-25.5, 138) * mm, "construction": true});
            skLineSegment(sketch, "E55.right", {"start": v(25.5, 46) * mm, "end": v(25.5, 138) * mm, "construction": true});
            skLineSegment(sketch, "E56.bottom", {"start": v(28.5, 46) * mm, "end": v(-28.5, 46) * mm});
            skLineSegment(sketch, "E56.top", {"start": v(28.5, 153) * mm, "end": v(-28.5, 153) * mm});
            skLineSegment(sketch, "E56.left", {"start": v(28.5, 46) * mm, "end": v(28.5, 153) * mm});
            skLineSegment(sketch, "E56.right", {"start": v(-28.5, 46) * mm, "end": v(-28.5, 153) * mm});
            skPoint(sketch, "E56.middle", {"position": v(0, 99.5) * mm});
            skSolve(sketch);
        }
        {
            var Q0;
            Q0 = qSketchRegion(id + "F40", true);
            extrude(context, id + "F41", {"entities" : qUnion([Q0]), "operationType" : NewBodyOperationType.ADD, "oppositeDirection" : true, "depth" : 30 * mm, "offsetDistance" : 25 * mm});
        }
        {
            var Q0;
            Q0=makeQuery(id+"F41.boolean.opBoolean","MERGE",FACE,{"derivedFrom":[makeQuery(id+"F9.opExtrude","CAP_FACE",FACE,{"disambiguationData":[OSD([sQuery(id+"F8.wireOp",EDGE,"E15.bottom"),sQuery(id+"F8.wireOp",EDGE,"E15.top"),sQuery(id+"F8.wireOp",EDGE,"E15.left"),sQuery(id+"F8.wireOp",EDGE,"E15.right"),sQuery(id+"F8.wireOp",EDGE,"E16.0"),sQuery(id+"F8.wireOp",EDGE,"E16.1"),sQuery(id+"F8.wireOp",EDGE,"E16.2"),sQuery(id+"F8.wireOp",EDGE,"E16.3")])],"isStart":false}),makeQuery(id+"F41.opExtrude","CAP_FACE",FACE,{"disambiguationData":[OSD([sQuery(id+"F40.wireOp",EDGE,"E56.bottom"),sQuery(id+"F40.wireOp",EDGE,"E56.top"),sQuery(id+"F40.wireOp",EDGE,"E56.left"),sQuery(id+"F40.wireOp",EDGE,"E56.right")])],"isStart":true})]});
            var sketch = newSketch(context, id + "F42", { "sketchPlane" : qUnion([Q0])});
            skPoint(sketch, "E57.orphan", {"position": v(-28.5, 46) * mm});
            skPoint(sketch, "E58.3.start.orphan", {"position": v(28.5, 46) * mm});
            skLineSegment(sketch, "E59", {"start": v(-25.5, 46) * mm, "end": v(25.5, 46) * mm});
            skLineSegment(sketch, "E60", {"start": v(25.5, 46) * mm, "end": v(25.5, 150) * mm});
            skLineSegment(sketch, "E61", {"start": v(25.5, 150) * mm, "end": v(-25.5, 150) * mm});
            skLineSegment(sketch, "E62", {"start": v(-25.5, 150) * mm, "end": v(-25.5, 46) * mm});
            skSolve(sketch);
        }
        {
            var Q0;
            Q0 = qSketchRegion(id + "F42", true);
            extrude(context, id + "F43", {"entities" : qUnion([Q0]), "operationType" : NewBodyOperationType.REMOVE, "oppositeDirection" : true, "depth" : 27 * mm, "offsetDistance" : 25 * mm});
        }
        {
            var Q0;
            Q0=makeQuery(id+"F41.opExtrude","CAP_FACE",FACE,{"disambiguationData":[OSD([sQuery(id+"F40.wireOp",EDGE,"E56.bottom"),sQuery(id+"F40.wireOp",EDGE,"E56.top"),sQuery(id+"F40.wireOp",EDGE,"E56.left"),sQuery(id+"F40.wireOp",EDGE,"E56.right")])],"isStart":false});
            var sketch = newSketch(context, id + "F44", { "sketchPlane" : qUnion([Q0])});
            skLineSegment(sketch, "E63.0.0", {"start": v(-28.5, -43) * mm, "end": v(-28.5, -153) * mm});
            skLineSegment(sketch, "E63.0.1", {"start": v(-28.5, -153) * mm, "end": v(28.5, -153) * mm});
            skLineSegment(sketch, "E63.0.2", {"start": v(28.5, -153) * mm, "end": v(28.5, -43) * mm});
            skLineSegment(sketch, "E63.0.3", {"start": v(28.5, -43) * mm, "end": v(-28.5, -43) * mm});
            skLineSegment(sketch, "E64.0", {"start": v(-25.5, -46) * mm, "end": v(-25.5, -150) * mm});
            skLineSegment(sketch, "E64.1", {"start": v(25.5, -46) * mm, "end": v(-25.5, -46) * mm});
            skLineSegment(sketch, "E64.2", {"start": v(25.5, -150) * mm, "end": v(25.5, -46) * mm});
            skLineSegment(sketch, "E64.3", {"start": v(-25.5, -150) * mm, "end": v(25.5, -150) * mm});
            skSolve(sketch);
        }
        {
            var Q0;
            Q0 = qSketchRegion(id + "F44", true);
            var Q1;
            Q1=makeQuery(id+"F14.opExtrude","CAP_FACE",FACE,{"disambiguationData":[OSD([sQuery(id+"F13.wireOp",EDGE,"E21.0.0"),sQuery(id+"F13.wireOp",EDGE,"E21.0.1"),sQuery(id+"F13.wireOp",EDGE,"E21.0.2"),sQuery(id+"F13.wireOp",EDGE,"E21.0.3"),sQuery(id+"F13.wireOp",EDGE,"E22.0"),sQuery(id+"F13.wireOp",EDGE,"E22.1"),sQuery(id+"F13.wireOp",EDGE,"E22.2"),sQuery(id+"F13.wireOp",EDGE,"E22.3")])],"isStart":false});
            extrude(context, id + "F45", {"entities" : qUnion([Q0]), "operationType" : NewBodyOperationType.ADD, "endBound" : BoundingType.UP_TO_SURFACE, "depth" : 20 * mm, "endBoundEntityFace" : qUnion([Q1]), "offsetDistance" : 25 * mm});
        }
    });
